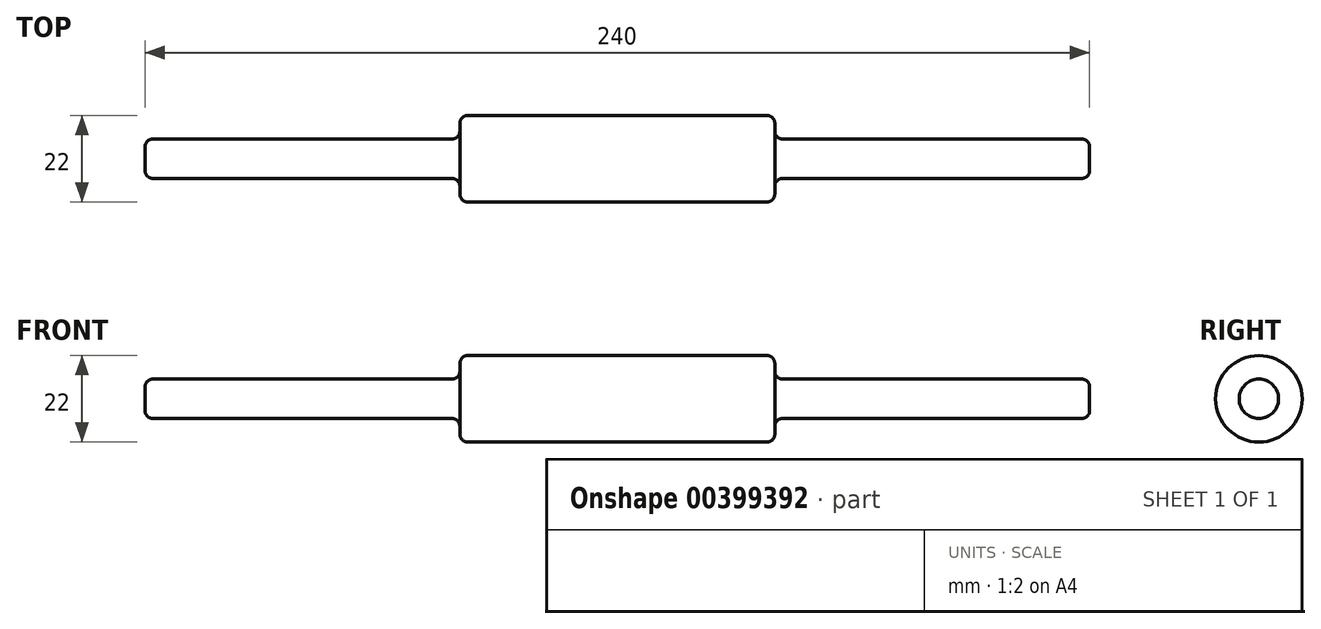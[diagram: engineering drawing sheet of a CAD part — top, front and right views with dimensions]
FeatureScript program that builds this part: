
annotation { "Feature Type Name" : "Feature", "Feature Type Description" : "" }
export const myFeature = defineFeature(function(context is Context, id is Id, definition is map)
    precondition{}
    {
        {
            var Q0;
            Q0=qCreatedBy(makeId("Right.planeOp"),FACE);
            var sketch = newSketch(context, id + "F0", { "sketchPlane" : qUnion([Q0])});
            skCircle(sketch, "E0", {"center": v(0, 0) * mm, "radius": 11 * mm});
            skCircle(sketch, "E1", {"center": v(0, 0) * mm, "radius": 5 * mm});
            skSolve(sketch);
        }
        {
            var Q0;
            Q0=makeQuery(id+"F0.imprint","IMPRINT",FACE,{"disambiguationData":[TD([[makeQuery(id+"F0.imprint","IMPRINT",EDGE,{"derivedFrom":sQuery(id+"F0.wireOp",EDGE,"E0")}),1.0]])]});
            var Q1;
            Q1=makeQuery(id+"F0.imprint","IMPRINT",FACE,{"disambiguationData":[TD([[makeQuery(id+"F0.imprint","IMPRINT",EDGE,{"derivedFrom":sQuery(id+"F0.wireOp",EDGE,"E1")}),1.0]])]});
            extrude(context, id + "F1", {"entities" : qUnion([Q0, Q1]), "endBound" : BoundingType.SYMMETRIC, "depth" : 80 * mm});
        }
        {
            var Q0;
            Q0=makeQuery(id+"F0.imprint","IMPRINT",FACE,{"disambiguationData":[TD([[makeQuery(id+"F0.imprint","IMPRINT",EDGE,{"derivedFrom":sQuery(id+"F0.wireOp",EDGE,"E1")}),1.0]])]});
            extrude(context, id + "F2", {"entities" : qUnion([Q0]), "operationType" : NewBodyOperationType.ADD, "endBound" : BoundingType.SYMMETRIC, "depth" : 240 * mm});
        }
        {
            var Q0;
            Q0=makeQuery(id+"F1.opExtrude","CAP_FACE",FACE,{"disambiguationData":[OSD([sQuery(id+"F0.wireOp",EDGE,"E0")])],"isStart":true});
            var Q1;
            Q1=makeQuery(id+"F1.opExtrude","CAP_FACE",FACE,{"disambiguationData":[OSD([sQuery(id+"F0.wireOp",EDGE,"E0")])],"isStart":false});
            var Q2;
            Q2=makeQuery(id+"F2.opExtrude","CAP_FACE",FACE,{"disambiguationData":[OSD([sQuery(id+"F0.wireOp",EDGE,"E1")])],"isStart":false});
            var Q3;
            Q3=makeQuery(id+"F2.opExtrude","CAP_EDGE",EDGE,{"disambiguationData":[OSD([sQuery(id+"F0.wireOp",EDGE,"E1")])],"isStart":true});
            fillet(context, id + "F3", {"entities" : qUnion([Q0, Q1, Q2, Q3]), "radius" : 2 * mm, "tangentPropagation" : true, "allowEdgeOverflow" : false});
        }
    });
